# Revit family: A301,A302,A303
name_source: partatom
category: Plumbing Fixtures
units: mm (PartAtom-declared; Revit-internal decimal feet)

## family parameters
Always vertical = Yes
Cut with Voids When Loaded = No
Part Type = Normal
Room Calculation Point = No
Round Connector Dimension = Use Diameter
Shared = No
Work Plane-Based = No

## types (3) — shared parameters
Design Country = Slovenia
Manufacturer Country = Slovenia
Manufacturer Name = HERZ/Unitas
Masterformat 2024 Code = 22 41 39
Masterformat 2024 Description = Residential Faucets, Supplies, and Trim
Material = Nickel chromium-plated
Product Group = Shower head
UNSPSC Code = 3018
URL = https://www.herz-taps.com
Uniclass 2015 Code = Pr_40_20_87
Uniclass 2015 Name = Taps and water supply outlet fittings
Uniformat II Code = D2010
Uniformat II Description = Plumbing Fixtures
Website 1 = www.unitas.rs
Website 2 = www.herz.rs
Website 3 = www.herz.eu

## per-type parameters (varying)
| type | Product Family | Product Name | Product SKU |
| a301 | Bella | 12055 Bella | 12055 |
| a302 | Simphony | 12054 Simphony | 12054 |
| a303 | Shower | 12057 Shower | 12057 |

## geometry (parser evidence)
native form markers: Sweep x3
no freeform markers — native parametric forms only
